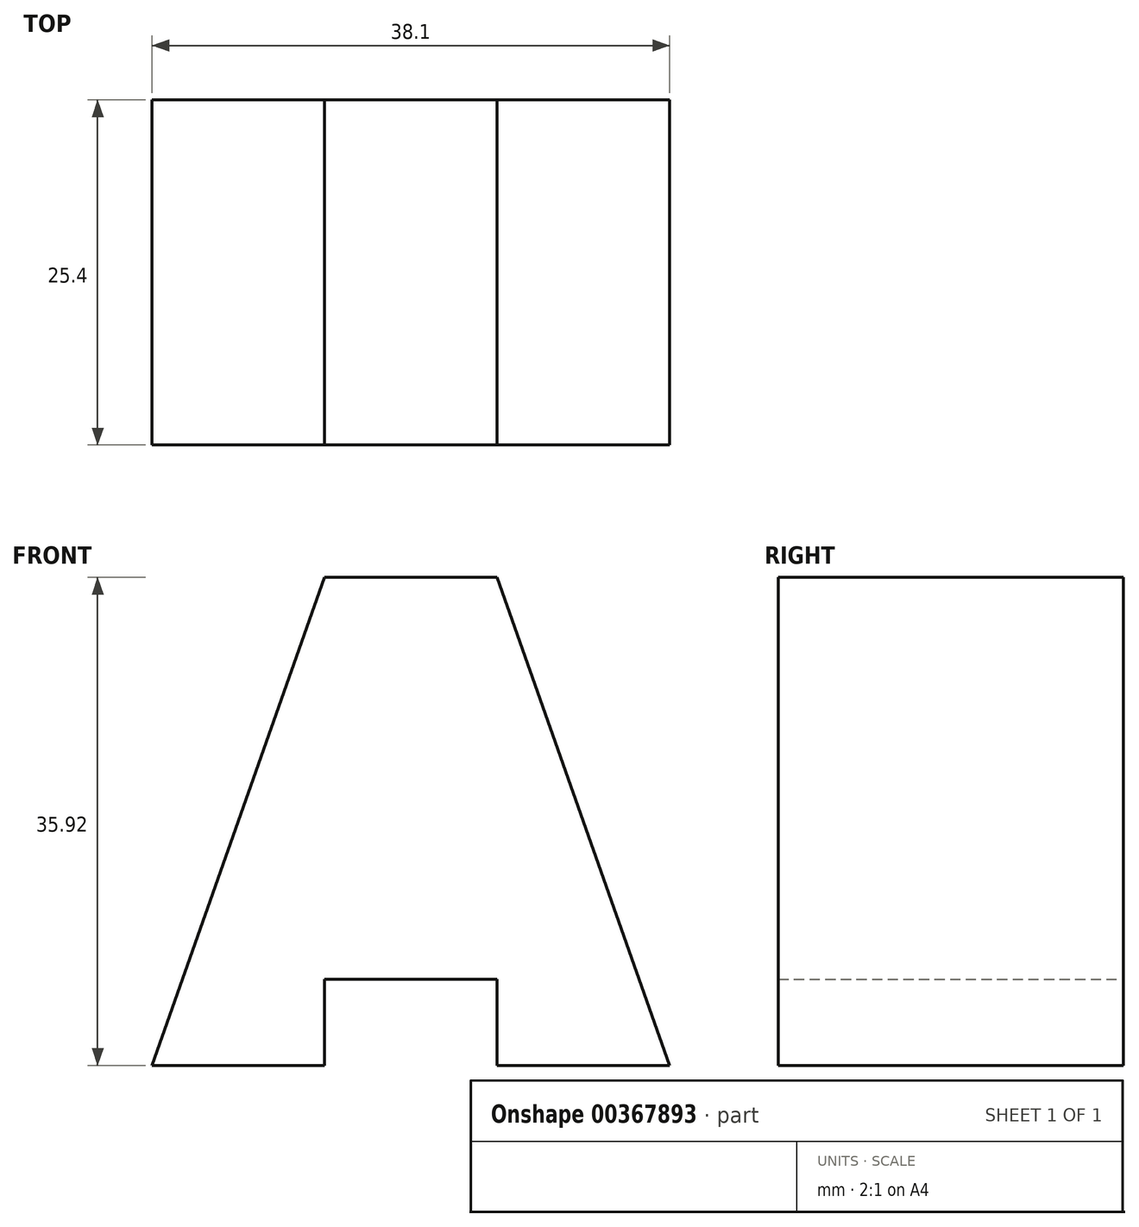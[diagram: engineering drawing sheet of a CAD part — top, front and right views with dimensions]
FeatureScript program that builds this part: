
annotation { "Feature Type Name" : "Feature", "Feature Type Description" : "" }
export const myFeature = defineFeature(function(context is Context, id is Id, definition is map)
    precondition{}
    {
        {
            var Q0;
            Q0=qCreatedBy(makeId("Front.planeOp"),FACE);
            var sketch = newSketch(context, id + "F0", { "sketchPlane" : qUnion([Q0])});
            skLineSegment(sketch, "E0", {"start": v(-16.74, 0) * mm, "end": v(-4.04, 0) * mm});
            skLineSegment(sketch, "E1", {"start": v(-4.04, 0) * mm, "end": v(-4.04, 6.35) * mm});
            skLineSegment(sketch, "E2", {"start": v(-4.04, 6.35) * mm, "end": v(8.66, 6.35) * mm});
            skLineSegment(sketch, "E3", {"start": v(8.66, 6.35) * mm, "end": v(8.66, 0) * mm});
            skLineSegment(sketch, "E4", {"start": v(8.66, 0) * mm, "end": v(21.36, 0) * mm});
            skLineSegment(sketch, "E5", {"start": v(-4.04, 35.92) * mm, "end": v(8.66, 35.92) * mm});
            skLineSegment(sketch, "E6", {"start": v(-4.04, 35.92) * mm, "end": v(-16.74, 0) * mm});
            skLineSegment(sketch, "E7", {"start": v(8.66, 35.92) * mm, "end": v(21.36, 0) * mm});
            skSolve(sketch);
        }
        {
            var Q0;
            Q0=makeQuery(id+"F0.imprint","IMPRINT",FACE,{"disambiguationData":[TD([[makeQuery(id+"F0.imprint","IMPRINT",EDGE,{"derivedFrom":sQuery(id+"F0.wireOp",EDGE,"E0")}),1.0]])]});
            extrude(context, id + "F1", {"entities" : qUnion([Q0]), "depth" : 25.4 * mm});
        }
    });
